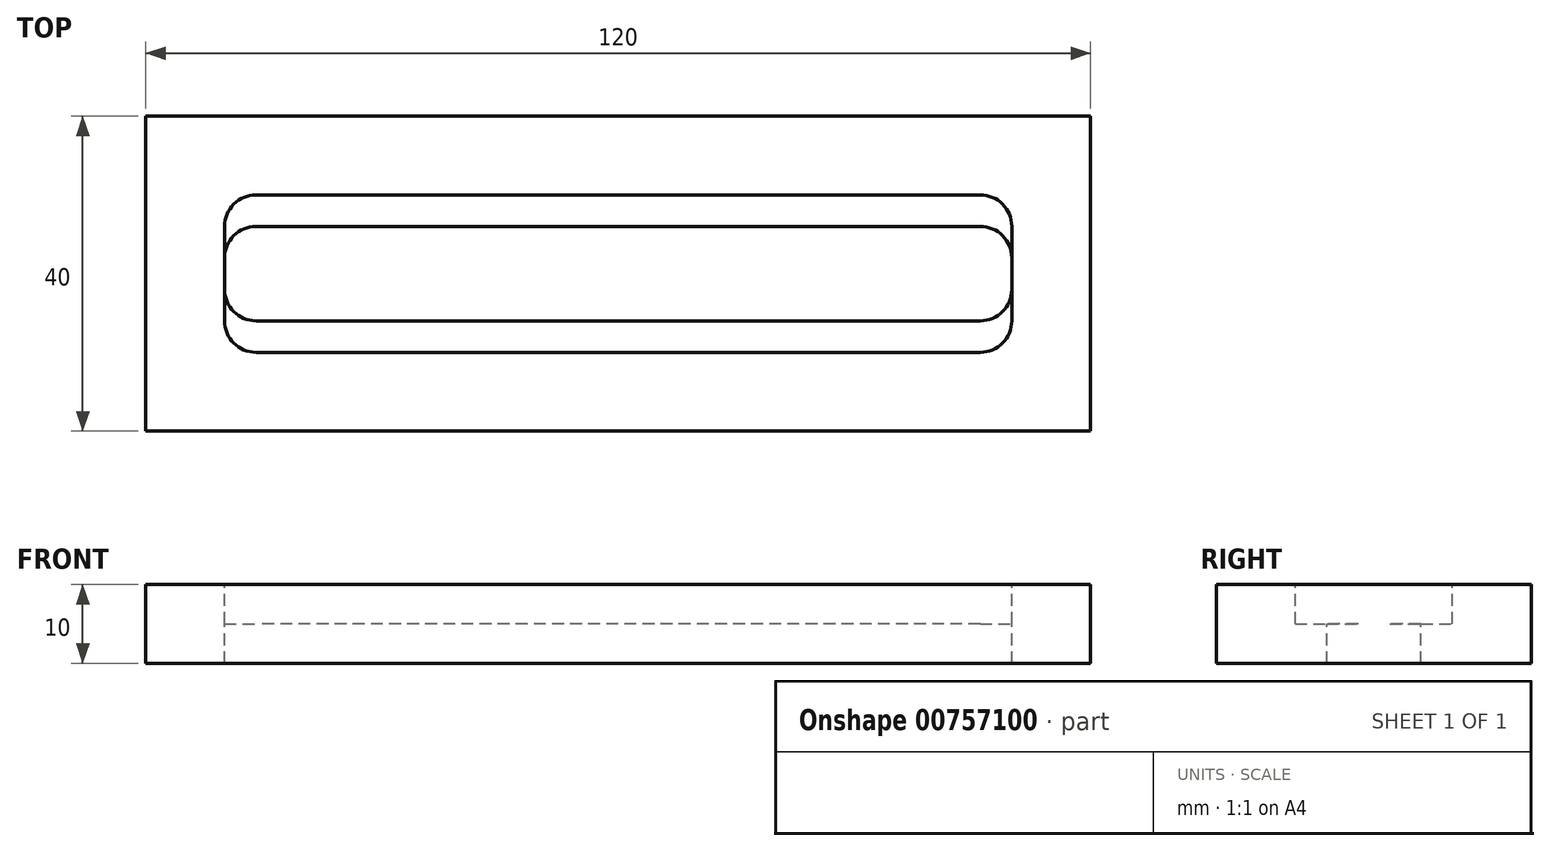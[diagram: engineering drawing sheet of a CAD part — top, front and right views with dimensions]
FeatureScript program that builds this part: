
annotation { "Feature Type Name" : "Feature", "Feature Type Description" : "" }
export const myFeature = defineFeature(function(context is Context, id is Id, definition is map)
    precondition{}
    {
        {
            var Q0;
            Q0=qCreatedBy(makeId("Top.planeOp"),FACE);
            var sketch = newSketch(context, id + "F0", { "sketchPlane" : qUnion([Q0])});
            skLineSegment(sketch, "E0.bottom", {"start": v(60, 20) * mm, "end": v(-60, 20) * mm});
            skLineSegment(sketch, "E0.top", {"start": v(60, -20) * mm, "end": v(-60, -20) * mm});
            skLineSegment(sketch, "E0.left", {"start": v(60, 20) * mm, "end": v(60, -20) * mm});
            skLineSegment(sketch, "E0.right", {"start": v(-60, 20) * mm, "end": v(-60, -20) * mm});
            skPoint(sketch, "E0.middle", {"position": v(0, 0) * mm});
            skSolve(sketch);
        }
        {
            var Q0;
            Q0=makeQuery(id+"F0.imprint","IMPRINT",FACE,{"disambiguationData":[TD([[makeQuery(id+"F0.imprint","IMPRINT",EDGE,{"derivedFrom":sQuery(id+"F0.wireOp",EDGE,"E0.bottom")}),1.0]])]});
            extrude(context, id + "F1", {"entities" : qUnion([Q0]), "depth" : 10 * mm, "offsetDistance" : 25 * mm});
        }
        {
            var Q0;
            Q0=makeQuery(id+"F1.opExtrude","CAP_FACE",FACE,{"disambiguationData":[OSD([sQuery(id+"F0.wireOp",EDGE,"E0.bottom"),sQuery(id+"F0.wireOp",EDGE,"E0.top"),sQuery(id+"F0.wireOp",EDGE,"E0.left"),sQuery(id+"F0.wireOp",EDGE,"E0.right")])],"isStart":false});
            var sketch = newSketch(context, id + "F2", { "sketchPlane" : qUnion([Q0])});
            skLineSegment(sketch, "E1.bottom", {"start": v(50, 10) * mm, "end": v(-50, 10) * mm});
            skLineSegment(sketch, "E1.top", {"start": v(50, -10) * mm, "end": v(-50, -10) * mm});
            skLineSegment(sketch, "E1.left", {"start": v(50, 10) * mm, "end": v(50, -10) * mm});
            skLineSegment(sketch, "E1.right", {"start": v(-50, 10) * mm, "end": v(-50, -10) * mm});
            skPoint(sketch, "E1.middle", {"position": v(0, 0) * mm});
            skSolve(sketch);
        }
        {
            var Q0;
            Q0=makeQuery(id+"F2.imprint","IMPRINT",FACE,{"disambiguationData":[TD([[makeQuery(id+"F2.imprint","IMPRINT",EDGE,{"derivedFrom":sQuery(id+"F2.wireOp",EDGE,"E1.bottom")}),1.0]])]});
            extrude(context, id + "F3", {"entities" : qUnion([Q0]), "operationType" : NewBodyOperationType.REMOVE, "oppositeDirection" : true, "depth" : 5 * mm, "offsetDistance" : 25 * mm});
        }
        {
            var Q0;
            Q0=makeQuery(id+"F3.boolean.opBoolean","COPY",EDGE,{"derivedFrom":makeQuery(id+"F3.opExtrude","SWEPT_EDGE",EDGE,{"disambiguationData":[OSD([sQuery(id+"F2.wireOp",EDGE,"E1.bottom"),sQuery(id+"F2.wireOp",EDGE,"E1.right")])]})});
            var Q1;
            Q1=makeQuery(id+"F3.boolean.opBoolean","COPY",EDGE,{"derivedFrom":makeQuery(id+"F3.opExtrude","SWEPT_EDGE",EDGE,{"disambiguationData":[OSD([sQuery(id+"F2.wireOp",EDGE,"E1.bottom"),sQuery(id+"F2.wireOp",EDGE,"E1.left")])]})});
            var Q2;
            Q2=makeQuery(id+"F3.boolean.opBoolean","COPY",EDGE,{"derivedFrom":makeQuery(id+"F3.opExtrude","SWEPT_EDGE",EDGE,{"disambiguationData":[OSD([sQuery(id+"F2.wireOp",EDGE,"E1.top"),sQuery(id+"F2.wireOp",EDGE,"E1.left")])]})});
            var Q3;
            Q3=makeQuery(id+"F3.boolean.opBoolean","COPY",EDGE,{"derivedFrom":makeQuery(id+"F3.opExtrude","SWEPT_EDGE",EDGE,{"disambiguationData":[OSD([sQuery(id+"F2.wireOp",EDGE,"E1.top"),sQuery(id+"F2.wireOp",EDGE,"E1.right")])]})});
            fillet(context, id + "F4", {"entities" : qUnion([Q0, Q1, Q2, Q3]), "radius" : 4 * mm, "tangentPropagation" : true, "allowEdgeOverflow" : false});
        }
        {
            var Q0;
            Q0=makeQuery(id+"F3.boolean.opBoolean","COPY",FACE,{"derivedFrom":makeQuery(id+"F3.opExtrude","CAP_FACE",FACE,{"disambiguationData":[OSD([sQuery(id+"F2.wireOp",EDGE,"E1.bottom"),sQuery(id+"F2.wireOp",EDGE,"E1.top"),sQuery(id+"F2.wireOp",EDGE,"E1.left"),sQuery(id+"F2.wireOp",EDGE,"E1.right")])],"isStart":false})});
            var sketch = newSketch(context, id + "F5", { "sketchPlane" : qUnion([Q0])});
            skLineSegment(sketch, "E2.bottom", {"start": v(50, 6) * mm, "end": v(-50, 6) * mm});
            skLineSegment(sketch, "E2.top", {"start": v(50, -6) * mm, "end": v(-50, -6) * mm});
            skLineSegment(sketch, "E2.left", {"start": v(50, 6) * mm, "end": v(50, -6) * mm});
            skLineSegment(sketch, "E2.right", {"start": v(-50, 6) * mm, "end": v(-50, -6) * mm});
            skPoint(sketch, "E2.middle", {"position": v(0, 0) * mm});
            skSolve(sketch);
        }
        {
            var Q0;
            Q0=makeQuery(id+"F5.imprint","IMPRINT",FACE,{"disambiguationData":[TD([[makeQuery(id+"F5.imprint","IMPRINT",EDGE,{"derivedFrom":sQuery(id+"F5.wireOp",EDGE,"E2.bottom")}),1.0]])]});
            extrude(context, id + "F6", {"entities" : qUnion([Q0]), "operationType" : NewBodyOperationType.REMOVE, "endBound" : BoundingType.UP_TO_NEXT, "oppositeDirection" : true, "depth" : 25 * mm, "offsetDistance" : 25 * mm});
        }
        {
            var Q0;
            Q0=makeQuery(id+"F6.boolean.opBoolean","COPY",EDGE,{"derivedFrom":makeQuery(id+"F6.opExtrude","SWEPT_EDGE",EDGE,{"disambiguationData":[OSD([sQuery(id+"F2.wireOp",EDGE,"E1.bottom"),sQuery(id+"F2.wireOp",EDGE,"E1.top"),sQuery(id+"F2.wireOp",EDGE,"E1.left"),sQuery(id+"F2.wireOp",EDGE,"E1.right"),sQuery(id+"F5.wireOp",EDGE,"E2.bottom"),sQuery(id+"F5.wireOp",EDGE,"E2.right")])]})});
            var Q1;
            Q1=makeQuery(id+"F6.boolean.opBoolean","COPY",EDGE,{"derivedFrom":makeQuery(id+"F6.opExtrude","SWEPT_EDGE",EDGE,{"disambiguationData":[OSD([sQuery(id+"F2.wireOp",EDGE,"E1.bottom"),sQuery(id+"F2.wireOp",EDGE,"E1.top"),sQuery(id+"F2.wireOp",EDGE,"E1.left"),sQuery(id+"F2.wireOp",EDGE,"E1.right"),sQuery(id+"F5.wireOp",EDGE,"E2.top"),sQuery(id+"F5.wireOp",EDGE,"E2.right")])]})});
            var Q2;
            Q2=makeQuery(id+"F6.boolean.opBoolean","COPY",EDGE,{"derivedFrom":makeQuery(id+"F6.opExtrude","SWEPT_EDGE",EDGE,{"disambiguationData":[OSD([sQuery(id+"F2.wireOp",EDGE,"E1.bottom"),sQuery(id+"F2.wireOp",EDGE,"E1.top"),sQuery(id+"F2.wireOp",EDGE,"E1.left"),sQuery(id+"F2.wireOp",EDGE,"E1.right"),sQuery(id+"F5.wireOp",EDGE,"E2.top"),sQuery(id+"F5.wireOp",EDGE,"E2.left")])]})});
            var Q3;
            Q3=makeQuery(id+"F6.boolean.opBoolean","COPY",EDGE,{"derivedFrom":makeQuery(id+"F6.opExtrude","SWEPT_EDGE",EDGE,{"disambiguationData":[OSD([sQuery(id+"F2.wireOp",EDGE,"E1.bottom"),sQuery(id+"F2.wireOp",EDGE,"E1.top"),sQuery(id+"F2.wireOp",EDGE,"E1.left"),sQuery(id+"F2.wireOp",EDGE,"E1.right"),sQuery(id+"F5.wireOp",EDGE,"E2.bottom"),sQuery(id+"F5.wireOp",EDGE,"E2.left")])]})});
            fillet(context, id + "F7", {"entities" : qUnion([Q0, Q1, Q2, Q3]), "radius" : 4 * mm, "tangentPropagation" : true, "allowEdgeOverflow" : false});
        }
    });
